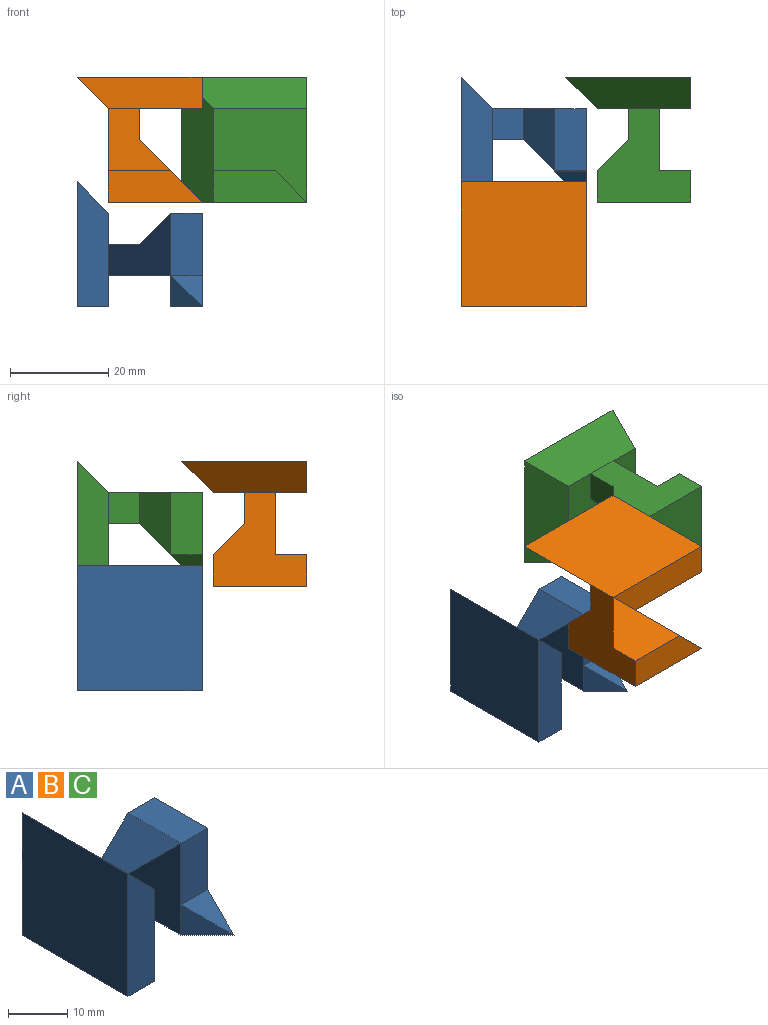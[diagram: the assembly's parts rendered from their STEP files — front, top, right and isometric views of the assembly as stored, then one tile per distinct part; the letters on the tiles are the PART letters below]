
ASSEMBLY  parts=3 mates=5
PART A: 17 faces, bbox 25.4x25.4x25.4 mm
  f0: plane 19.05x12.7mm, normal (-1,0,0), area 161.3mm2, adj f2,f9,f13,f14,f16
  f1: plane 6.35x6.35mm, normal (0,-0.71,0.71), area 28.5mm2, adj f13,f15,f16
  f2: plane 19.05x19.05mm, normal (0,1,0), area 221.8mm2, adj f0,f8,f9,f10,f11,f12,f14,f15
  f3: plane 25.4x6.35mm, normal (0,-1,0), area 141.1mm2, adj f4,f5,f6,f7
  f4: plane 25.4x6.35mm, normal (0,0,-1), area 141.1mm2, adj f3,f5,f6,f8
  f5: plane 19.05x19.05mm, normal (1,0,0), area 342.7mm2, adj f3,f4,f7,f8,f9,f11
  f6: plane 25.4x25.4mm, normal (-1,0,0), area 645.2mm2, adj f3,f4,f7,f8
  f7: plane 25.4x6.35mm, normal (0.71,0,0.71), area 199.6mm2, adj f3,f5,f6,f8
  f8: plane 25.4x6.35mm, normal (0.71,0.71,0), area 199.6mm2, adj f2,f4,f5,f6,f7
  f9: plane 12.7x12.7mm, normal (0,-0.71,-0.71), area 142.6mm2, adj f0,f2,f5,f10,f11
  f10: plane 12.7x6.35mm, normal (-0.71,0,0.71), area 85.5mm2, adj f2,f9,f11,f12
  f11: plane 6.35x6.35mm, normal (0,0,1), area 40.3mm2, adj f2,f5,f9,f10
  f12: plane 12.7x6.35mm, normal (0,0,1), area 80.6mm2, adj f2,f10,f13,f15
  f13: plane 12.7x6.35mm, normal (0,-1,0), area 80.6mm2, adj f0,f1,f12,f15
  f14: plane 19.05x6.35mm, normal (0,0,-1), area 100.8mm2, adj f0,f2,f15,f16
  f15: plane 19.05x19.05mm, normal (1,0,0), area 262.1mm2, adj f1,f2,f12,f13,f14
  f16: plane 6.35x6.35mm, normal (-0.71,-0.71,0), area 28.5mm2, adj f0,f1,f14
PART B: same geometry as A
PART C: same geometry as A
PLACE A at identity fixed
PLACE B rot(axis=(-0.58,0.58,0.58),120deg) t=(12.7,-21.3,34)mm
PLACE C rot(axis=(0.58,-0.58,-0.58),120deg) t=(34,12.7,21.3)mm
MATE planar A.f0 <-> B.f13  axis (-1,0,0) through (19.05,-1.06,-5.82)mm
MATE planar A.f10 <-> C.f9  axis (-0.71,0,0.71) through (16.23,1.41,3.53)mm
MATE planar B.f5 <-> C.f2  axis (0,0,-1) through (16.31,-24.54,27.65)mm
MATE planar A.f13 <-> C.f0  axis (0,-1,0) through (22.22,-6.35,0)mm
MATE planar A.f9 <-> B.f10  axis (0,-0.71,-0.71) through (13.55,2.12,-2.12)mm
